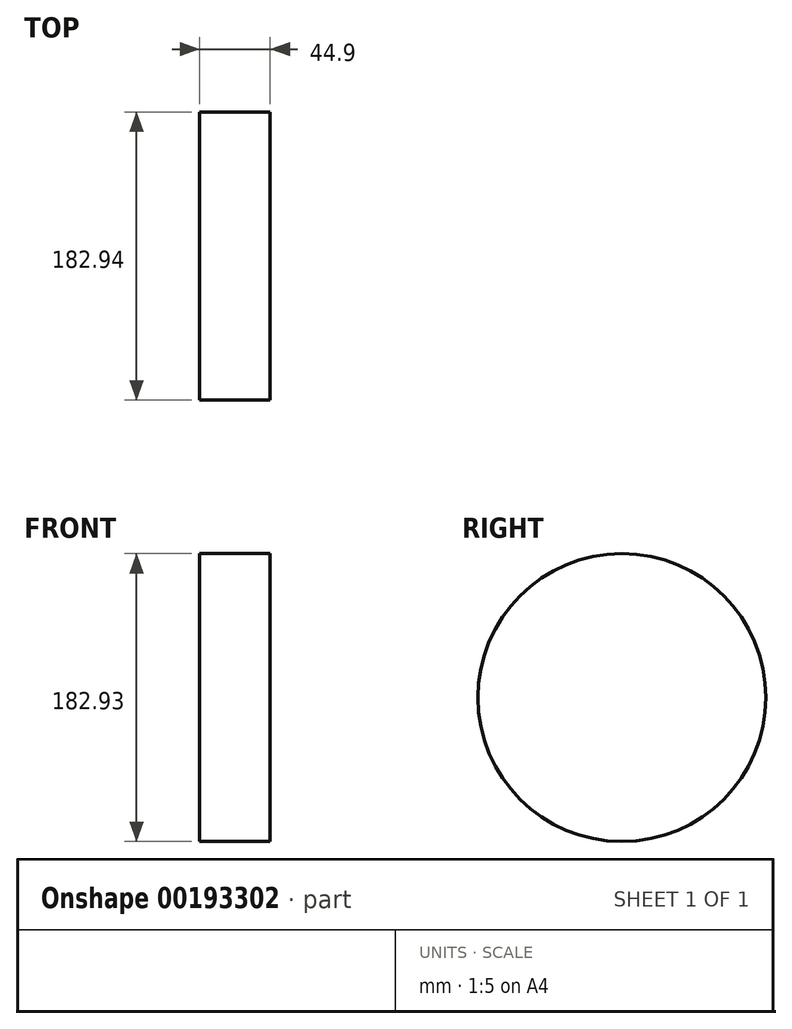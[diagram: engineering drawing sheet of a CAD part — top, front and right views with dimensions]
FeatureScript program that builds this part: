
annotation { "Feature Type Name" : "Feature", "Feature Type Description" : "" }
export const myFeature = defineFeature(function(context is Context, id is Id, definition is map)
    precondition{}
    {
        {
            var Q0;
            Q0=qCreatedBy(makeId("Front.planeOp"),FACE);
            var sketch = newSketch(context, id + "F0", { "sketchPlane" : qUnion([Q0])});
            skLineSegment(sketch, "E0.bottom", {"start": v(-56.82, 47.78) * mm, "end": v(-11.92, 47.78) * mm});
            skLineSegment(sketch, "E0.top", {"start": v(-56.82, -43.68) * mm, "end": v(-11.92, -43.68) * mm});
            skLineSegment(sketch, "E0.left", {"start": v(-56.82, 47.78) * mm, "end": v(-56.82, -43.68) * mm});
            skLineSegment(sketch, "E0.right", {"start": v(-11.92, 47.78) * mm, "end": v(-11.92, -43.68) * mm});
            skSolve(sketch);
        }
        {
            var Q0;
            Q0=makeQuery(id+"F0.imprint","IMPRINT",FACE,{"disambiguationData":[TD([[makeQuery(id+"F0.imprint","IMPRINT",EDGE,{"derivedFrom":sQuery(id+"F0.wireOp",EDGE,"E0.bottom")}),-1.0]])]});
            var Q1;
            Q1=sQuery(id+"F0.wireOp",EDGE,"E0.top");
            revolve(context, id + "F1", {"entities" : qUnion([Q0]), "axis" : qUnion([Q1]), "revolveType" : RevolveType.FULL});
        }
    });
